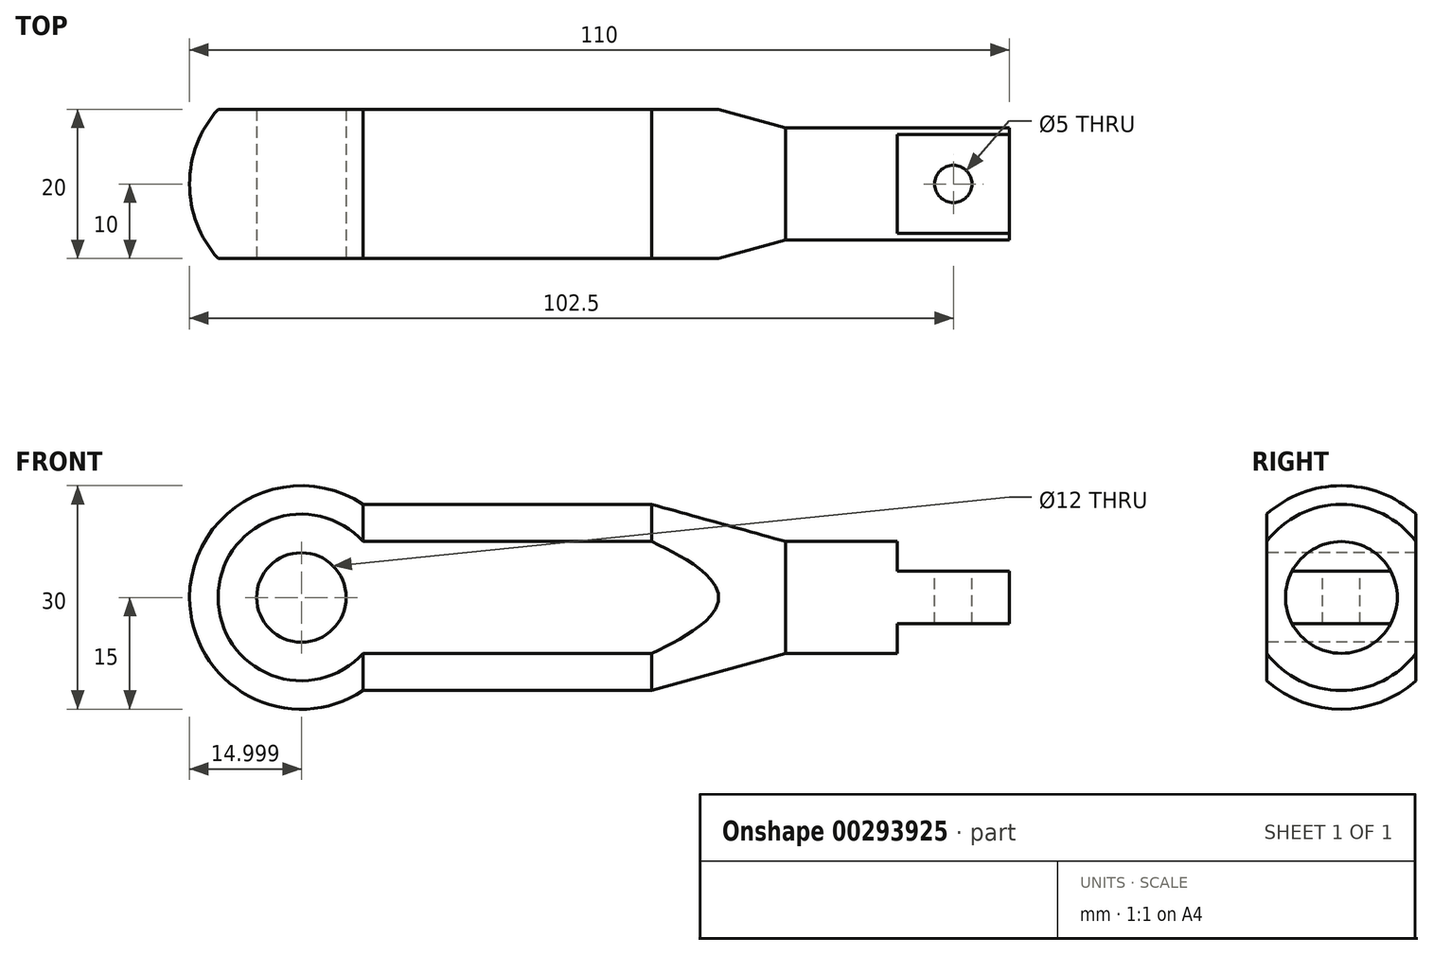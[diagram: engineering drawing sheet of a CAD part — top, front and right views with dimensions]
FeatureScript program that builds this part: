
annotation { "Feature Type Name" : "Feature", "Feature Type Description" : "" }
export const myFeature = defineFeature(function(context is Context, id is Id, definition is map)
    precondition{}
    {
        {
            var Q0;
            Q0=qCreatedBy(makeId("Front.planeOp"),FACE);
            var sketch = newSketch(context, id + "F0", { "sketchPlane" : qUnion([Q0])});
            skLineSegment(sketch, "E0", {"start": v(-160.36, 0) * mm, "end": v(185.25, 0) * mm, "construction": true});
            skArc(sketch, "E1", {"start": v(-5.25, 12.5) * mm, "mid": v(-20.63, 13.22) * mm, "end": v(-28.54, 0) * mm});
            skLineSegment(sketch, "E2", {"start": v(-5.25, 12.5) * mm, "end": v(33.46, 12.5) * mm});
            skLineSegment(sketch, "E3", {"start": v(33.46, 12.5) * mm, "end": v(51.46, 7.5) * mm});
            skLineSegment(sketch, "E4", {"start": v(51.46, 7.5) * mm, "end": v(81.46, 7.5) * mm});
            skLineSegment(sketch, "E5", {"start": v(81.46, 7.5) * mm, "end": v(81.46, 0) * mm});
            skLineSegment(sketch, "E6", {"start": v(81.46, 0) * mm, "end": v(-28.54, 0) * mm});
            skLineSegment(sketch, "E7", {"start": v(-28.54, 0) * mm, "end": v(81.46, 0) * mm});
            skSolve(sketch);
        }
        {
            var Q0;
            Q0 = qSketchRegion(id + "F0", true);
            var Q1;
            Q1=sQuery(id+"F0.wireOp",EDGE,"E0");
            revolve(context, id + "F1", {"entities" : qUnion([Q0]), "axis" : qUnion([Q1]), "revolveType" : RevolveType.FULL});
        }
        {
            var Q0;
            Q0=makeQuery(id+"F1.opRevolve","SWEPT_FACE",FACE,{"disambiguationData":[OSD([sQuery(id+"F0.wireOp",EDGE,"E5")])]});
            var sketch = newSketch(context, id + "F2", { "sketchPlane" : qUnion([Q0])});
            skArc(sketch, "E8", {"start": v(-9.44, -3.5) * mm, "mid": v(0, -10.07) * mm, "end": v(9.44, -3.5) * mm});
            skLineSegment(sketch, "E9", {"start": v(-9.44, 3.5) * mm, "end": v(9.44, 3.5) * mm});
            skLineSegment(sketch, "E10", {"start": v(9.44, -3.5) * mm, "end": v(-9.44, -3.5) * mm});
            skArc(sketch, "E11.trimOffspring", {"start": v(9.44, 3.5) * mm, "mid": v(0, 10.07) * mm, "end": v(-9.44, 3.5) * mm});
            skSolve(sketch);
        }
        {
            var Q0;
            Q0 = qSketchRegion(id + "F2", true);
            extrude(context, id + "F3", {"entities" : qUnion([Q0]), "operationType" : NewBodyOperationType.REMOVE, "oppositeDirection" : true, "depth" : 15 * mm});
        }
        {
            var Q0;
            Q0=makeQuery(id+"F3.boolean.opBoolean","COPY",FACE,{"derivedFrom":makeQuery(id+"F3.opExtrude","SWEPT_FACE",FACE,{"disambiguationData":[OSD([sQuery(id+"F2.wireOp",EDGE,"E9")])]})});
            var sketch = newSketch(context, id + "F4", { "sketchPlane" : qUnion([Q0])});
            skCircle(sketch, "E12", {"center": v(73.96, 0) * mm, "radius": 2.5 * mm});
            skSolve(sketch);
        }
        {
            var Q0;
            Q0 = qSketchRegion(id + "F4", true);
            extrude(context, id + "F5", {"entities" : qUnion([Q0]), "operationType" : NewBodyOperationType.REMOVE, "oppositeDirection" : true, "depth" : 25 * mm});
        }
        {
            var Q0;
            Q0=makeQuery(id+"F1.opRevolve","SWEPT_FACE",FACE,{"disambiguationData":[OSD([sQuery(id+"F0.wireOp",EDGE,"E5")])]});
            var sketch = newSketch(context, id + "F6", { "sketchPlane" : qUnion([Q0])});
            skArc(sketch, "E13", {"start": v(-10, 11.18) * mm, "mid": v(-15, 0) * mm, "end": v(-10, -11.18) * mm});
            skLineSegment(sketch, "E14", {"start": v(-10, 11.18) * mm, "end": v(-10, -11.18) * mm});
            skLineSegment(sketch, "E15", {"start": v(10, 11.18) * mm, "end": v(10, -11.18) * mm});
            skLineSegment(sketch, "E16", {"start": v(10, 0) * mm, "end": v(10, 6.9) * mm});
            skArc(sketch, "E17.trimOffspring", {"start": v(10, -11.18) * mm, "mid": v(15, 0) * mm, "end": v(10, 11.18) * mm});
            skSolve(sketch);
        }
        {
            var Q0;
            Q0 = qSketchRegion(id + "F6", true);
            extrude(context, id + "F7", {"entities" : qUnion([Q0]), "operationType" : NewBodyOperationType.REMOVE, "oppositeDirection" : true, "depth" : 130 * mm});
        }
        {
            var Q0;
            Q0=makeQuery(id+"F7.boolean.opBoolean","COPY",FACE,{"derivedFrom":makeQuery(id+"F7.opExtrude","SWEPT_FACE",FACE,{"disambiguationData":[OSD([sQuery(id+"F6.wireOp",EDGE,"E14")])]})});
            var sketch = newSketch(context, id + "F8", { "sketchPlane" : qUnion([Q0])});
            skCircle(sketch, "E18", {"center": v(-13.54, 0) * mm, "radius": 6 * mm});
            skSolve(sketch);
        }
        {
            var Q0;
            Q0=makeQuery(id+"F8.imprint","IMPRINT",FACE,{"disambiguationData":[TD([[makeQuery(id+"F8.imprint","IMPRINT",EDGE,{"derivedFrom":sQuery(id+"F8.wireOp",EDGE,"E18")}),1.0]])]});
            extrude(context, id + "F9", {"entities" : qUnion([Q0]), "operationType" : NewBodyOperationType.REMOVE, "oppositeDirection" : true, "depth" : 50 * mm});
        }
    });
